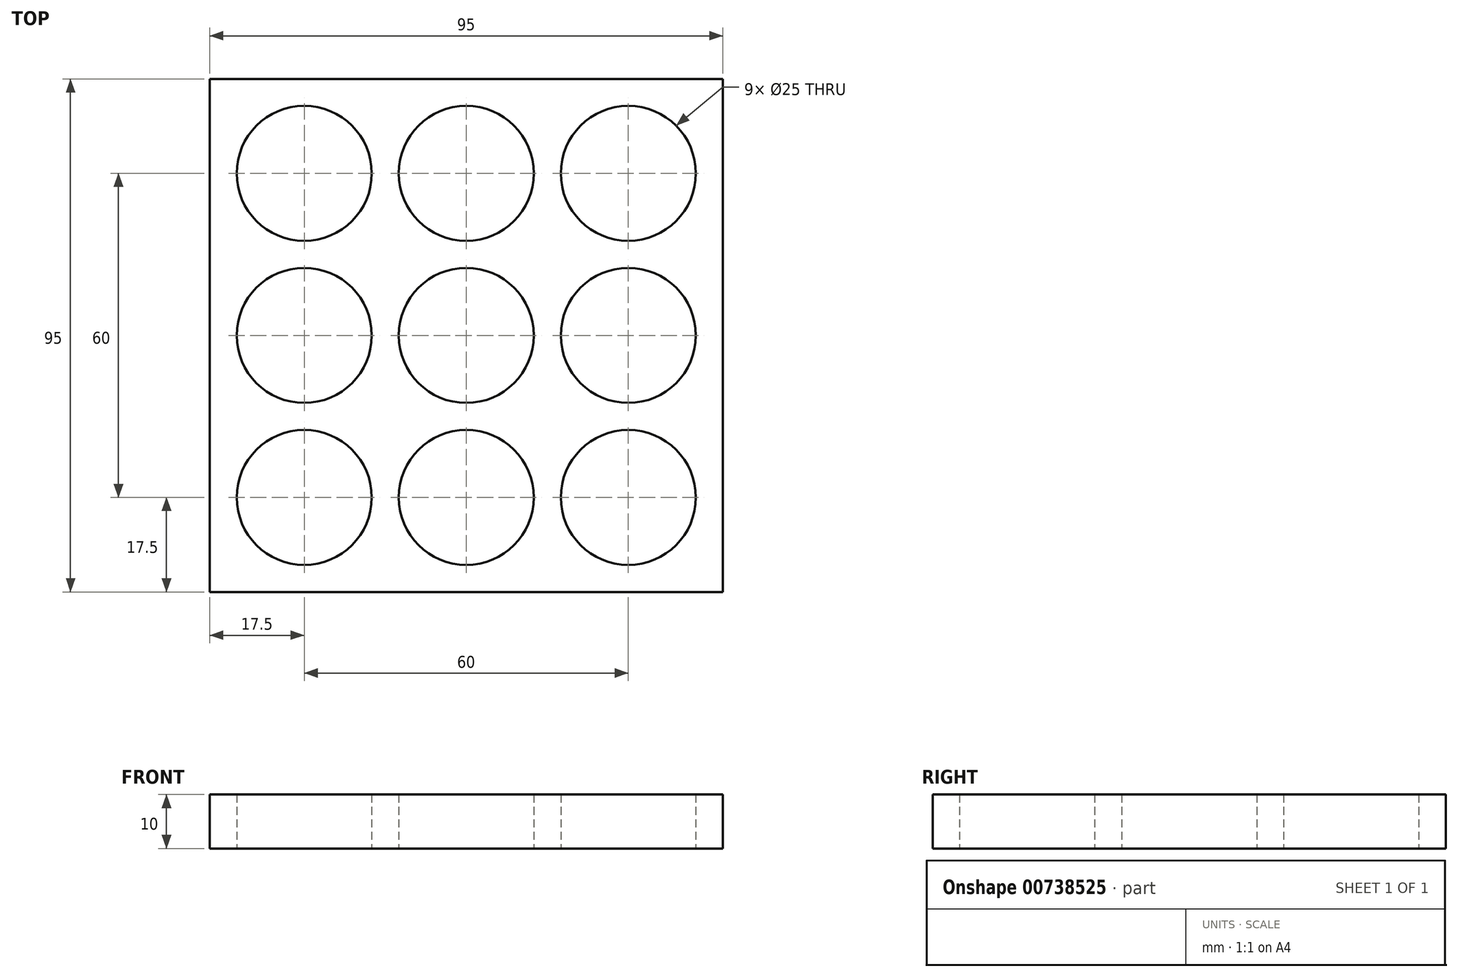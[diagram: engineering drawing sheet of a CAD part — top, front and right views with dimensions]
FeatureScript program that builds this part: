
annotation { "Feature Type Name" : "Feature", "Feature Type Description" : "" }
export const myFeature = defineFeature(function(context is Context, id is Id, definition is map)
    precondition{}
    {
        {
            var Q0;
            Q0=qCreatedBy(makeId("Top.planeOp"),FACE);
            var sketch = newSketch(context, id + "F0", { "sketchPlane" : qUnion([Q0])});
            skCircle(sketch, "E0", {"center": v(0, 0) * mm, "radius": 12.5 * mm});
            skCircle(sketch, "E1", {"center": v(0, -30) * mm, "radius": 12.5 * mm});
            skCircle(sketch, "E2", {"center": v(-30, -30) * mm, "radius": 12.5 * mm});
            skCircle(sketch, "E3", {"center": v(-30, 0) * mm, "radius": 12.5 * mm});
            skCircle(sketch, "E4", {"center": v(-30, 30) * mm, "radius": 12.5 * mm});
            skCircle(sketch, "E5", {"center": v(0, 30) * mm, "radius": 12.5 * mm});
            skCircle(sketch, "E6", {"center": v(30, 30) * mm, "radius": 12.5 * mm});
            skCircle(sketch, "E7", {"center": v(30, 0) * mm, "radius": 12.5 * mm});
            skCircle(sketch, "E8", {"center": v(30, -30) * mm, "radius": 12.5 * mm});
            skLineSegment(sketch, "E9.0", {"start": v(47.5, 47.5) * mm, "end": v(-47.5, 47.5) * mm});
            skLineSegment(sketch, "E10.0", {"start": v(47.5, -47.5) * mm, "end": v(-47.5, -47.5) * mm});
            skLineSegment(sketch, "E11.0", {"start": v(47.5, 47.5) * mm, "end": v(47.5, -47.5) * mm});
            skLineSegment(sketch, "E12.0", {"start": v(-47.5, -47.5) * mm, "end": v(-47.5, 47.5) * mm});
            skPoint(sketch, "E13.orphan", {"position": v(-62.5, 30) * mm});
            skPoint(sketch, "E14.orphan", {"position": v(0, -62.5) * mm});
            skPoint(sketch, "E15.orphan", {"position": v(-62.5, -30) * mm});
            skPoint(sketch, "E16.orphan", {"position": v(62.5, 62.5) * mm});
            skPoint(sketch, "E17.orphan", {"position": v(62.5, -62.5) * mm});
            skPoint(sketch, "E18.end.orphan", {"position": v(-62.5, -62.5) * mm});
            skPoint(sketch, "E19.0.start.orphan", {"position": v(62.5, 30) * mm});
            skPoint(sketch, "E20.orphan", {"position": v(62.5, 0) * mm});
            skPoint(sketch, "E21.0.start.orphan", {"position": v(62.5, -30) * mm});
            skSolve(sketch);
        }
        {
            var Q0;
            Q0=qSketchRegion(id+"F0",true);
            extrude(context, id + "F1", {"entities" : qUnion([Q0]), "depth" : 10 * mm, "offsetDistance" : 25 * mm});
        }
    });
